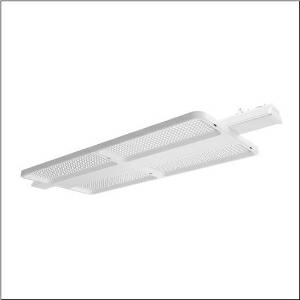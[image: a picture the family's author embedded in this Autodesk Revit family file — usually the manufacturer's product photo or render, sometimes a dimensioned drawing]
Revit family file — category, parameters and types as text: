
# Revit family: highbay_11_fur_licross_r__tragschiene_maxi_51hn12db5mla_0182
name_source: partatom
category: Lighting Fixtures
units: mm (PartAtom-declared; Revit-internal decimal feet)

## family parameters
Cut with Voids When Loaded = No
Host = Face
Light Source = No
Part Type = Normal
Room Calculation Point = No
Round Connector Dimension = Use Diameter
Shared = No

## types (1)
- --- (1 x LED, 29840 lm, 146.4 W, 5000K)
    Apparent Load = 146 VA
    CIE Flux Codes = 87 98 100 100 100
    Color Rendering = 80
    Color Temperature = 5000K
    Default Elevation = 1800 mm
    Description = high bay luminaire Highbay 11 for Licross® trunking rail maxi; direct symmetric wide distribution, light control with lens of PMMA; UGR ≤ 22 (X = 4H | Y = 8H | S = 0.25H | reflection values 70/50/20); luminous flux: 29.840lm; light colour: 850, colour temperature: 5000K, MacAdam ≤ 2 SDCM (initial), colour rendering: CRI > 80; luminous efficacy: 203,8lm/W; rated service life: 100.000h (L95/B50) at AT= 25°C; control: DALI 2; luminaire connection: plug, 5-pole, with phase selectionmains connection: 230..240V, AC 50/60Hz; connected load: 146,4W; protection rating (complete): IP64; insulation class (complete): insulation class I (protective earthing); protection symbol: D; impact resistance: IK07; certification: CE, ENEC, VDE, UKCA; internal wiring halogen-free; luminaire LABS conformity tested according to VDMA 24364:2018-05; corresponds to IFS (International Featured Standards) requirements for safety and quality in the food industry; housing frame of high-performance plastic PA6, matt traffic white (RAL 9016); cover of PMMA; fixing on rail side of steel, galvanised, white; blank cover of PC/ABS, traffic white (RAL 9016); dimension (LxWxH): 1.250 x 442 x 71mm; permissible operating ambient temperature: -45..+55°C (reducing of maximum allowable ambient temperature of 5°C with ceiling mounting); packaging unit: 1 piece
    Height = 72 mm  [stored 0.23622 ft]
    Lamp = 1 x LED
    Lamp Light Flux = 29840 lm
    Lamp Power = 146.4 W
    Lamp count = 1
    Length = 946 mm
    Luminous efficacy = 204 lm/W
    Manufacturer = Siteco
    ModVariant = No
    Model = 51HN12DB5MLA
    Mounting Place = Ceiling
    Mounting Type = Pendant
    Number of Poles = 1
    OnlyDefault = Yes
    Power Factor = 1
    Product Name = Highbay 11 für Licross® Tragschiene maxi
    Product group = high bay luminaire
    ProductGroupID = 901
    Protection Class = Protection class I
    Protection Degree = IP 64
    RLX_Detail_Level = 1
    RLX_Emergency_Light_Flux = 0 lm
    RLX_Emergency_Type = 0
    RLX_Emergency_Type_DB = No
    RlxData = <blob elided: 24225 chars, md5=7342e59b>
    Socket = socket
    Standby Power = 0 W
    System Light Flux = 29841 lm
    System Power = 146 W
    Type Comments = factory setting: luminous flux: 100 % | dim-lin: 254 | 678 mA
    Type Image = l_1361711.jpg
    URL = http://relux.com
    VarID = @adj_007221
    Voltage = 0 V
    Weight = 0.00 kg
    Width = 442 mm

note: [stored X ft] marks values corroborated as IEEE doubles in the binary element streams (Revit-internal decimal feet)

## geometry (parser evidence)
native form markers: Blend x4, Sweep x10
no freeform markers — native parametric forms only
